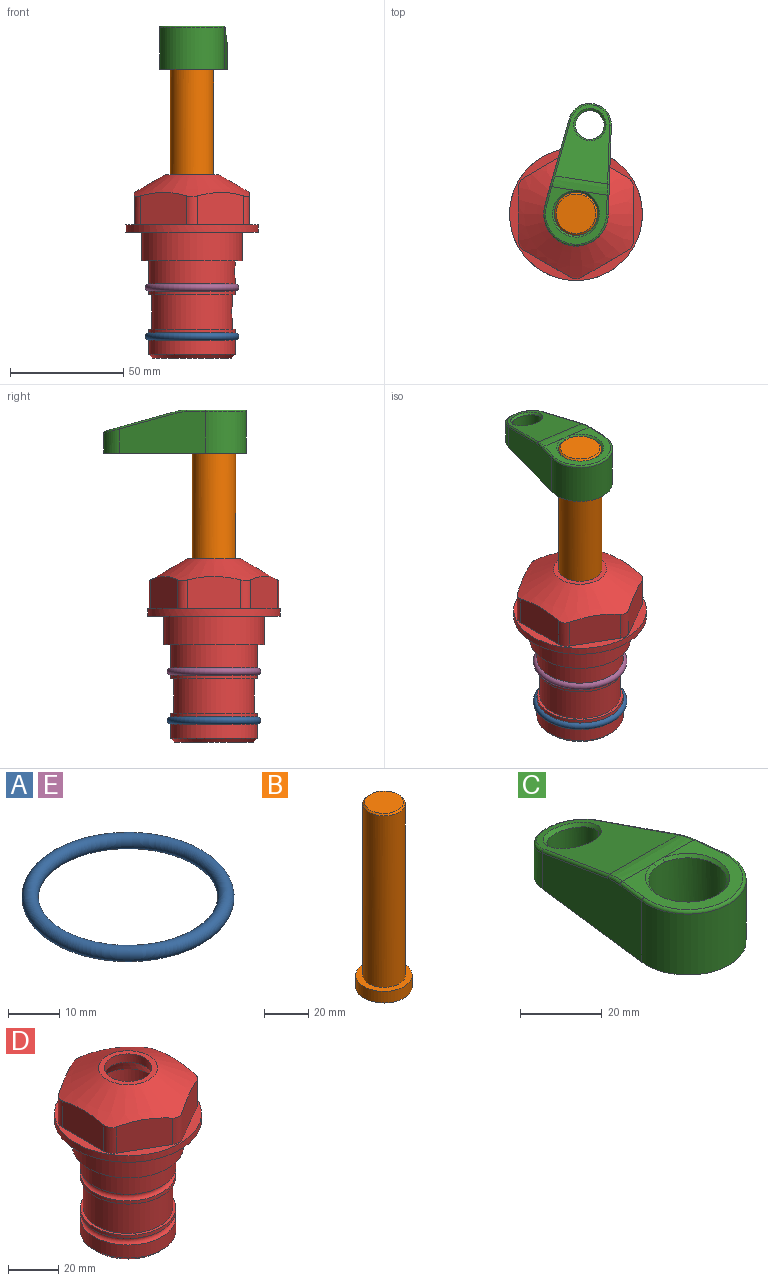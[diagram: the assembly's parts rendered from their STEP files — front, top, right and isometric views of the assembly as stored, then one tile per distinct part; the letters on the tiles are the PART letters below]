
ASSEMBLY  parts=5 mates=4
PART A: 1 faces, bbox 44.7x44.7x3.2 mm
  f0: torus R=19.05mm, axis (0,0,1), area 1193.9mm2
PART B: 6 faces, bbox 25.4x25.4x101.6 mm
  f0: plane 17.46x17.46mm, normal (0,0,1), area 239.5mm2, adj f5
  f1: plane 25.4x25.4mm, normal (0,0,-1), area 506.7mm2, adj f2
  f2: cylinder r=12.7mm len=25.4mm, axis (0,0,1), area 506.7mm2, adj f1,f3
  f3: plane 25.4x25.4mm, normal (0,0,1), area 221.7mm2, adj f2,f4
  f4: cylinder r=9.53mm len=94.46mm, axis (0,0,1), area 5653mm2, adj f3,f5
  f5: cone r=8.73mm half-angle=45deg, axis (0,0,-1), area 64.4mm2, adj f0,f4
PART C: 31 faces, bbox 31.7x65.5x19.8 mm
  f0: plane 39.12x18.26mm, normal (0.99,0.12,0), area 612.2mm2, adj f1,f4,f7,f11,f13,f15
  f1: cylinder r=9.53mm len=18.91mm, axis (0,0,-1), area 296.1mm2, adj f0,f2,f7,f17
  f2: plane 39.12x18.26mm, normal (-0.99,0.12,0), area 612.2mm2, adj f1,f4,f7,f12,f14,f16
  f3: cylinder r=6.35mm len=12.7mm, axis (0,0,-1), area 362.4mm2, adj f7,f18
  f4: cylinder r=14.29mm len=28.58mm, axis (0,0,-1), area 882.2mm2, adj f0,f2,f7,f10
  f5: cylinder r=9.53mm len=19.05mm, axis (0,0,-1), area 1092.6mm2, adj f7,f19,f20
  f6: plane 26.99x23.69mm, normal (0,0,1), area 216.2mm2, adj f9,f10,f11,f12,f19
  f7: plane 63.5x28.58mm, normal (0,0,-1), area 661.8mm2, adj f0,f1,f2,f3,f4,f5,f22,f23
  f8: plane 33.52x23.6mm, normal (0,0.26,0.97), area 486mm2, adj f9,f15,f16,f17,f18
  f9: cylinder r=19.05mm len=24.72mm, axis (1,0,0), area 120.4mm2, adj f6,f8,f13,f14,f20
  f10: torus R=13.49mm, axis (0,0,1), area 59mm2, adj f4,f6,f11,f12
  f11: cylinder r=0.79mm len=8.67mm, axis (0.12,-0.99,0), area 10.8mm2, adj f0,f6,f10,f13
  f12: cylinder r=0.79mm len=8.67mm, axis (0.12,0.99,0), area 10.8mm2, adj f2,f6,f10,f14
  f13: bspline ~4.95x1.42mm, area 6.1mm2, adj f0,f9,f11,f15
  f14: bspline ~4.95x1.42mm, area 6.1mm2, adj f2,f9,f12,f16
  f15: cylinder r=0.79mm len=25.95mm, axis (0.12,-0.96,0.26), area 32.9mm2, adj f0,f8,f13,f17
  f16: cylinder r=0.79mm len=25.95mm, axis (0.12,0.96,-0.26), area 32.9mm2, adj f2,f8,f14,f17
  f17: bspline ~18.91x8.38mm, area 30mm2, adj f1,f8,f15,f16
  f18: bspline ~14.29x14.29mm, area 48.3mm2, adj f3,f8
  f19: cone r=9.53mm half-angle=45deg, axis (0,0,1), area 66.5mm2, adj f5,f6,f20
  f20: bspline ~3.22x0.96mm, area 3.5mm2, adj f5,f9,f19
  f21: plane 2.75x2.72mm, normal (0,0,-1), area 2.9mm2, adj f23,f25,f28
  f22: plane 23.05x15.88mm, normal (-0.99,-0.12,0), area 323.6mm2, adj f7,f25,f26,f27,f28,f29
  f23: plane 23.05x15.88mm, normal (0.99,-0.12,0), area 323.6mm2, adj f7,f21,f25,f27,f28,f30
  f24: cylinder r=9.53mm len=10.69mm, axis (0,0,-1), area 114.7mm2, adj f7,f27,f29,f30
  f25: cylinder r=12.7mm len=20.59mm, axis (0,0,-1), area 381.1mm2, adj f7,f21,f22,f23,f26,f28
  f26: plane 2.75x2.72mm, normal (0,0,-1), area 2.9mm2, adj f22,f25,f28
  f27: plane 19.72x18.37mm, normal (0,-0.26,-0.97), area 291.8mm2, adj f22,f23,f24,f28,f29,f30
  f28: cylinder r=15.88mm len=19.92mm, axis (1,0,0), area 54.8mm2, adj f21,f22,f23,f25,f26,f27
  f29: cylinder r=1.59mm len=11mm, axis (0,0,-1), area 34.7mm2, adj f7,f22,f24,f27
  f30: cylinder r=1.59mm len=11mm, axis (0,0,-1), area 34.7mm2, adj f7,f23,f24,f27
PART D: 36 faces, bbox 58.7x58.7x81 mm
  f0: cylinder r=17.78mm len=35.56mm, axis (0,0,1), area 1670.8mm2, adj f23,f24,f31
  f1: cylinder r=19.05mm len=38.1mm, axis (0,0,1), area 1191.9mm2, adj f26,f27,f30
  f2: plane 58.66x58.66mm, normal (0,0,-1), area 1150.6mm2, adj f3,f28
  f3: cylinder r=29.33mm len=58.66mm, axis (0,0,-1), area 585.1mm2, adj f2,f4
  f4: plane 58.66x58.66mm, normal (0,0,1), area 475.9mm2, adj f3,f5,f6,f7,f8,f9,f10,f11
  f5: plane 20.32x14.34mm, normal (-0.5,0.87,0), area 324.4mm2, adj f4,f15,f16,f17
  f6: plane 20.32x14.34mm, normal (0.5,0.87,0), area 324.4mm2, adj f4,f14,f15,f17
  f7: plane 23.48x14.34mm, normal (1,0,0), area 324.4mm2, adj f4,f13,f14,f17
  f8: plane 20.32x14.34mm, normal (0.5,-0.87,0), area 324.4mm2, adj f4,f12,f13,f17
  f9: plane 20.32x14.34mm, normal (-0.5,-0.87,0), area 324.4mm2, adj f4,f11,f12,f17
  f10: plane 23.48x14.34mm, normal (-1,0,0), area 324.4mm2, adj f4,f11,f16,f17
  f11: cylinder r=5.08mm len=12.85mm, axis (0,0,-1), area 67.2mm2, adj f4,f9,f10,f17
  f12: cylinder r=5.08mm len=12.85mm, axis (0,0,-1), area 67.2mm2, adj f4,f8,f9,f17
  f13: cylinder r=5.08mm len=12.85mm, axis (0,0,-1), area 67.2mm2, adj f4,f7,f8,f17
  f14: cylinder r=5.08mm len=12.85mm, axis (0,0,-1), area 67.2mm2, adj f4,f6,f7,f17
  f15: cylinder r=5.08mm len=12.85mm, axis (0,0,-1), area 67.2mm2, adj f4,f5,f6,f17
  f16: cylinder r=5.08mm len=12.85mm, axis (0,0,-1), area 67.2mm2, adj f4,f5,f10,f17
  f17: cone r=11.73mm half-angle=60deg, axis (0,0,-1), area 2071.8mm2, adj f5,f6,f7,f8,f9,f10,f11,f12
  f18: plane 23.46x23.46mm, normal (0,0,1), area 147.4mm2, adj f17,f35
  f19: plane 34.93x34.93mm, normal (0,0,-1), area 958mm2, adj f29
  f20: cylinder r=19.05mm len=38.1mm, axis (0,0,1), area 760.1mm2, adj f21,f29
  f21: torus R=19.05mm, axis (0,0,1), area 565.3mm2, adj f20,f22
  f22: cylinder r=19.05mm len=38.1mm, axis (0,0,1), area 190mm2, adj f21,f23
  f23: plane 38.1x38.1mm, normal (0,0,1), area 146.9mm2, adj f0,f22
  f24: plane 38.1x38.1mm, normal (0,0,-1), area 146.9mm2, adj f0,f25
  f25: cylinder r=19.05mm len=38.1mm, axis (0,0,1), area 190mm2, adj f24,f26
  f26: torus R=19.05mm, axis (0,0,1), area 565.3mm2, adj f1,f25
  f27: plane 44.45x44.45mm, normal (0,0,-1), area 411.7mm2, adj f1,f28
  f28: cylinder r=22.23mm len=44.45mm, axis (0,0,1), area 1773.5mm2, adj f2,f27
  f29: cone r=19.05mm half-angle=45deg, axis (0,0,1), area 257.5mm2, adj f19,f20
  f30: cylinder r=3.17mm len=6.75mm, axis (-1,0,0), area 128mm2, adj f1,f33
  f31: cylinder r=3.17mm len=6.35mm, axis (-1,0,0), area 102.5mm2, adj f0,f33
  f32: plane 25.4x25.4mm, normal (0,0,1), area 506.7mm2, adj f33
  f33: cylinder r=12.7mm len=66.42mm, axis (0,0,-1), area 5236.2mm2, adj f30,f31,f32,f34
  f34: cone r=9.53mm half-angle=30deg, axis (0,0,-1), area 443.4mm2, adj f33,f35
  f35: cylinder r=9.53mm len=19.05mm, axis (0,0,-1), area 240.9mm2, adj f18,f34
PART E: same geometry as A
PLACE A t=(0,0,-21.59)mm
PLACE B rot(axis=(0,0,-1),8.8deg) t=(0,0,27.55)mm
PLACE C rot(axis=(0,0,-1),8.8deg) t=(0,0,27.55)mm
PLACE D at identity fixed
PLACE E at identity
MATE fastened D.f0 <-> A.f0  axis (0,0,1) through (0,0,-46.1)mm
MATE cylindrical D.f0 <-> B.f2  axis (0,0,1) through (0,0,-50.55)mm
MATE fastened D.f0 <-> E.f0  axis (0,0,1) through (0,0,-24.51)mm
MATE fastened B.f2 <-> C.f4  axis (0,0,1) through (0,0,91.05)mm
